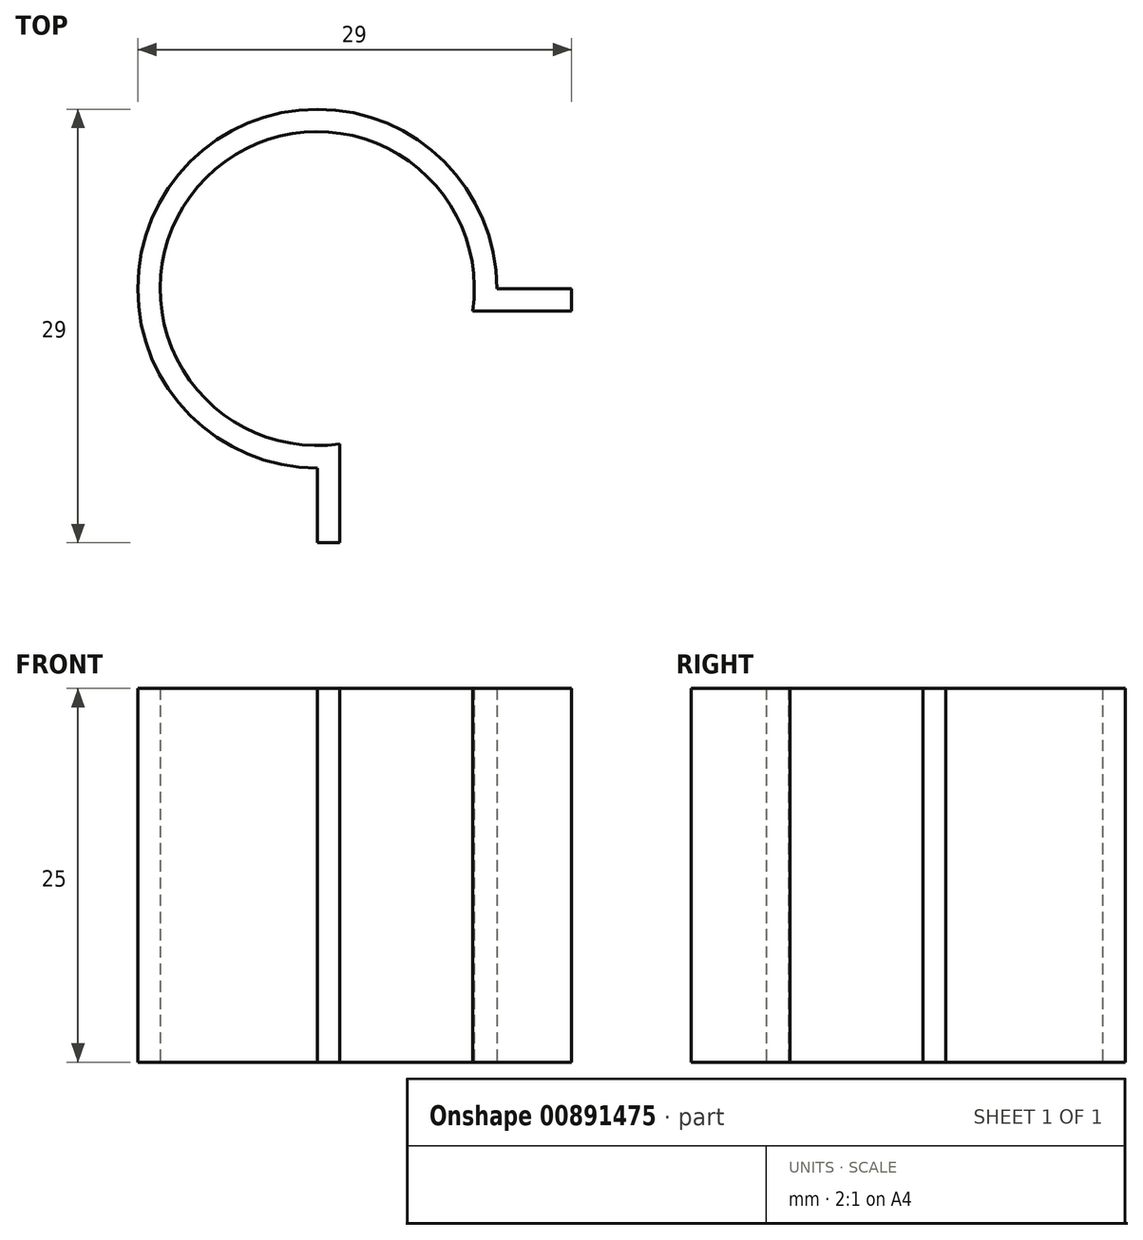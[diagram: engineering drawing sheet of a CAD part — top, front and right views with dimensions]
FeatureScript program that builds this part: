
annotation { "Feature Type Name" : "Feature", "Feature Type Description" : "" }
export const myFeature = defineFeature(function(context is Context, id is Id, definition is map)
    precondition{}
    {
        {
            var Q0;
            Q0=qCreatedBy(makeId("Top.planeOp"),FACE);
            var sketch = newSketch(context, id + "F0", { "sketchPlane" : qUnion([Q0])});
            skCircle(sketch, "E0", {"center": v(0, 0) * mm, "radius": 10.5 * mm});
            skCircle(sketch, "E1", {"center": v(0, 0) * mm, "radius": 12 * mm});
            skLineSegment(sketch, "E2.bottom", {"start": v(0, 0) * mm, "end": v(17, 0) * mm});
            skLineSegment(sketch, "E2.top", {"start": v(0, -17) * mm, "end": v(17, -17) * mm});
            skLineSegment(sketch, "E2.left", {"start": v(0, 0) * mm, "end": v(0, -17) * mm});
            skLineSegment(sketch, "E2.right", {"start": v(17, 0) * mm, "end": v(17, -17) * mm});
            skLineSegment(sketch, "E3.bottom", {"start": v(17, -17) * mm, "end": v(1.5, -17) * mm});
            skLineSegment(sketch, "E3.top", {"start": v(17, -1.5) * mm, "end": v(1.5, -1.5) * mm});
            skLineSegment(sketch, "E3.left", {"start": v(17, -17) * mm, "end": v(17, -1.5) * mm});
            skLineSegment(sketch, "E3.right", {"start": v(1.5, -17) * mm, "end": v(1.5, -1.5) * mm});
            skSolve(sketch);
        }
        {
            var Q0;
            {var subQ0=sQuery(id+"F0.wireOp",EDGE,"E2.left");var subQ1=sQuery(id+"F0.wireOp",EDGE,"E0");var subQ2=makeQuery(id+"F0.imprint","INTERSECT",VERTEX,{"derivedFrom":[subQ1,subQ0]});Q0=makeQuery(id+"F0.imprint","IMPRINT",FACE,{"disambiguationData":[TD([[makeQuery(id+"F0.imprint","IMPRINT",EDGE,{"disambiguationData":[TD([[subQ2,1.0]])],"derivedFrom":subQ1}),-1.0]])]});}
            var Q1;
            {var subQ0=sQuery(id+"F0.wireOp",EDGE,"E2.bottom");var subQ1=sQuery(id+"F0.wireOp",EDGE,"E0");var subQ2=makeQuery(id+"F0.imprint","INTERSECT",VERTEX,{"derivedFrom":[subQ1,subQ0]});Q1=makeQuery(id+"F0.imprint","IMPRINT",FACE,{"disambiguationData":[TD([[makeQuery(id+"F0.imprint","IMPRINT",EDGE,{"disambiguationData":[TD([[subQ2,1.0]])],"derivedFrom":subQ1}),-1.0]])]});}
            var Q2;
            {var subQ5=sQuery(id+"F0.wireOp",EDGE,"E2.right");Q2=makeQuery(id+"F0.imprint","IMPRINT",FACE,{"disambiguationData":[TD([[makeQuery(id+"F0.imprint","IMPRINT",EDGE,{"derivedFrom":subQ5}),-1.0]])]});}
            var Q3;
            {var subQ0=sQuery(id+"F0.wireOp",EDGE,"E2.left");var subQ1=sQuery(id+"F0.wireOp",EDGE,"E0");var subQ2=makeQuery(id+"F0.imprint","INTERSECT",VERTEX,{"derivedFrom":[subQ1,subQ0]});Q3=makeQuery(id+"F0.imprint","IMPRINT",FACE,{"disambiguationData":[TD([[makeQuery(id+"F0.imprint","IMPRINT",EDGE,{"disambiguationData":[TD([[subQ2,-1.0]])],"derivedFrom":subQ1}),-1.0]])]});}
            var Q4;
            {var subQ5=sQuery(id+"F0.wireOp",EDGE,"E2.top");Q4=makeQuery(id+"F0.imprint","IMPRINT",FACE,{"disambiguationData":[TD([[makeQuery(id+"F0.imprint","IMPRINT",EDGE,{"derivedFrom":subQ5}),1.0]])]});}
            extrude(context, id + "F1", {"entities" : qUnion([Q0, Q1, Q2, Q3, Q4]), "depth" : 25 * mm, "offsetDistance" : 25 * mm});
        }
    });
